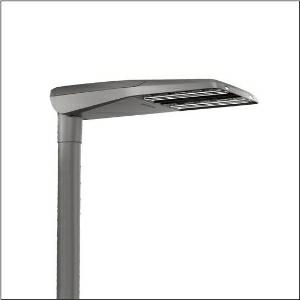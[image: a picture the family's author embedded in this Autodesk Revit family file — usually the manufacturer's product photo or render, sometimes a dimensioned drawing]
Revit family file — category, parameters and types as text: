
# Revit family: streetlight_sl_11_iq_midi___pc-r_5xc3f51f08me_381f
name_source: partatom
category: Lighting Fixtures
units: mm (PartAtom-declared; Revit-internal decimal feet)

## family parameters
Cut with Voids When Loaded = No
Host = Face
Light Source = No
Part Type = Normal
Room Calculation Point = No
Round Connector Dimension = Use Diameter
Shared = No

## types (1)
- --- (1 x LED, 15540 lm, 124.7 W, 3000K)
    Apparent Load = 125 VA
    CIE Flux Codes = 37 73 96 100 100
    Color Rendering = 70
    Color Temperature = 3000K
    Default Elevation = 1800 mm
    Description = Streetlight SL 11 iQ midi, mast luminaire, primary light control with 3 zone facetted reflector, of plastic, silver coated, highly specular, primary optical cover: cover, of PMMA, transparent, light distribution: PC-R, light emission: direct distribution, primary light characteristic: asymmetric, installation type: post-top, side-entry, LED, High Power LED, rated luminous flux: 15.540lm, luminous efficacy: 125lm/W, light colour: 730, colour temperature: 3000K, control: Street-Remote, optimised constant luminous flux control (CLO 2.0), Desk-Remote (wireless, voltage-free reading and setting of iQ features in the workshop via application-optimized NFC function/RFID function), Light-Fading, Smart-Wire, Night-Set, Lumen-Switch, Temp-Guard, Auto-Match, with cable H07RN-F 5x 1.5mm², mains connection: 220..240V, AC, 50/60Hz, connection cable pre-assembled, cable length: 12,5m, start of lifetime: 125W, end of lifetime: 132W, reduction: 57W, luminaire housing, of diecast aluminium, powder-coated, Siteco® metallic grey (DB 702S), length: 780mm, width: 376mm, height: 118mm, spigot size: 60/76mm (post-top) and 42/60/76mm (side-entry), mast flange for spigot size: 42mm: 5XC10008XM4, 60mm: 5XC10008XM2, 76/60mm: 5XC10108XM1, equipment: Power, protection rating (complete): IP66, insulation class (complete): insulation class II (safety insulation), certification: CE, ENEC, VDE, impact resistance: IK09, permissible operating ambient temperature for outdoor applications: -25..+50°C, standard-compliant lighting for roads and squares, packaging unit: 1 piece

Light Distribution: PC-R
    Height = 118 mm
    Lamp = 1 x LED
    Lamp Light Flux = 15540 lm
    Lamp Power = 124.7 W
    Lamp count = 1
    Length = 780 mm
    Luminous efficacy = 125 lm/W
    Manufacturer = Siteco
    ModVariant = No
    Model = 5XC3F51F08ME
    Number of Poles = 1
    OnlyDefault = Yes
    Power Factor = 1
    Product Name = Streetlight SL 11 iQ midi | PC-R
    Product group = mast luminaire | pylon top
    ProductGroupID = 6100
    Protection Class = Protection class II
    Protection Degree = IP 66
    RLX_Detail_Level = 1
    RlxData = <blob elided: 74185 chars, md5=a00a28f0>
    Socket = socket
    Standby Power = 0 W
    System Light Flux = 15540 lm
    System Power = 125 W
    Type Comments = factory setting: luminous flux: 100 % | dim-lin: 254 | 557 mA
    Type Image = l_1005960.jpg
    URL = http://relux.com
    VarID = @adj_117627
    Voltage = 0 V
    Weight = 0.00 kg
    Width = 376 mm

## geometry (parser evidence)
native form markers: Blend x4, Sweep x10
no freeform markers — native parametric forms only
